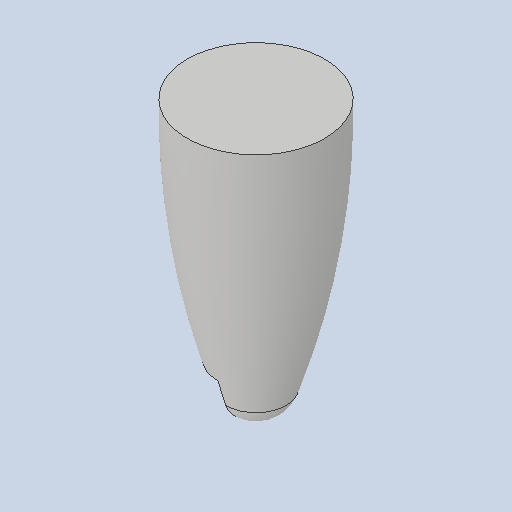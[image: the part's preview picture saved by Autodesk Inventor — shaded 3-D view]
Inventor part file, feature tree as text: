
AUTODESK INVENTOR PART (.ipt)
format: ipt  version: 2025 (Build 290162010, 162A)  size: 136,192 bytes
history: native  units: mm
features: sketch x3, revolve x2, projected_geometry x2, other x1, extrude x1
ambient origin geometry x8: Origin, YZ Plane, XZ Plane, XY Plane, X Axis, Y Axis, Z Axis, Center Point
bodies: Body1 (feature_tree)
feature tree (9):
  other  "Твердое тело1"
  revolve  "Вращение1"
  revolve  "Вращение2"
  extrude  "Выдавливание1"  Depth=100.0mm
  sketch  "Эскиз1"
  sketch  "Эскиз2"
  projected_geometry  "Спроецированная петля1"
  projected_geometry  "Спроецированная петля2"
  sketch  "Эскиз3"
